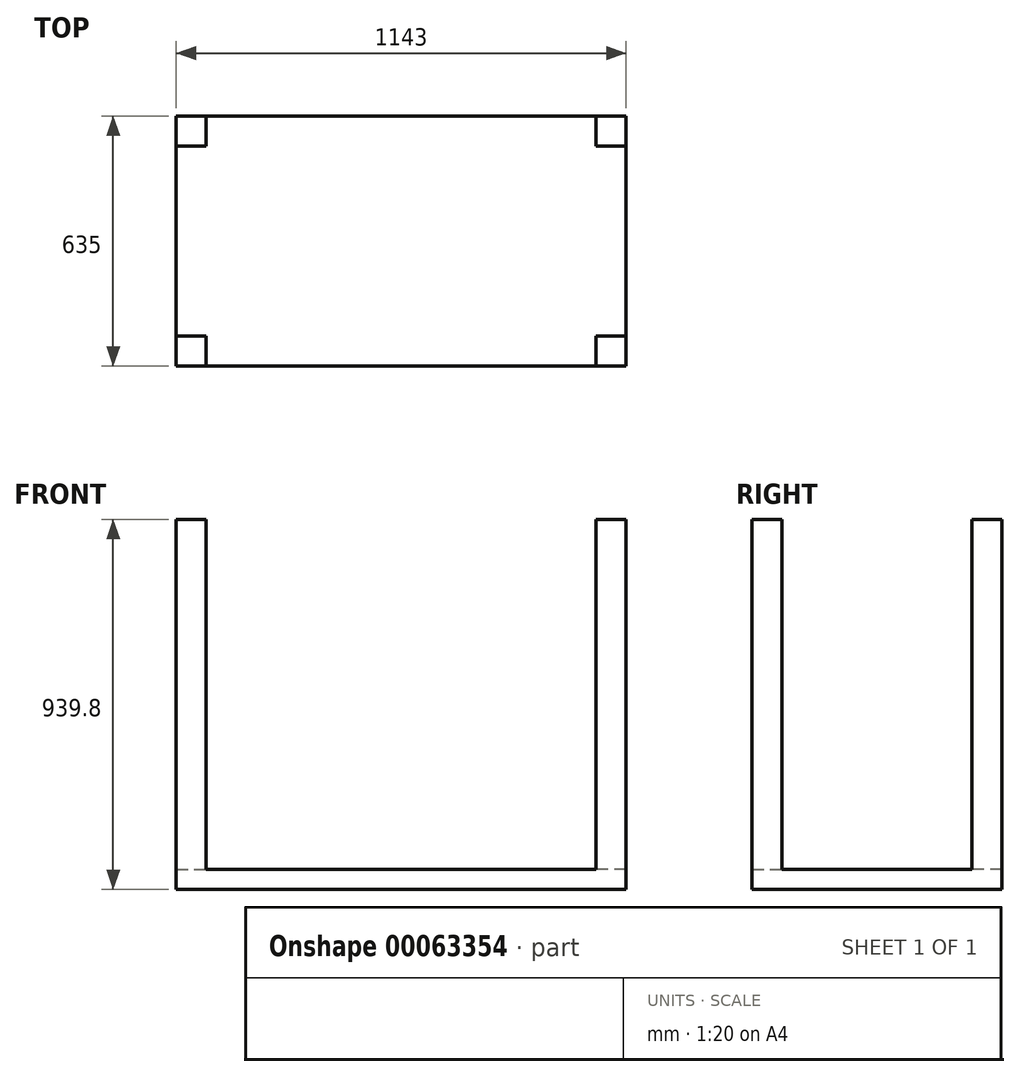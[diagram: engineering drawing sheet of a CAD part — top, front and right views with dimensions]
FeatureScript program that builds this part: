
annotation { "Feature Type Name" : "Feature", "Feature Type Description" : "" }
export const myFeature = defineFeature(function(context is Context, id is Id, definition is map)
    precondition{}
    {
        {
            var Q0;
            Q0=qCreatedBy(makeId("Top.planeOp"),FACE);
            var sketch = newSketch(context, id + "F0", { "sketchPlane" : qUnion([Q0])});
            skLineSegment(sketch, "E0.rect.bottom", {"start": v(571.5, 317.5) * mm, "end": v(-571.5, 317.5) * mm});
            skLineSegment(sketch, "E0.rect.top", {"start": v(571.5, -317.5) * mm, "end": v(-571.5, -317.5) * mm});
            skLineSegment(sketch, "E0.rect.left", {"start": v(571.5, 317.5) * mm, "end": v(571.5, -317.5) * mm});
            skLineSegment(sketch, "E0.rect.right", {"start": v(-571.5, 317.5) * mm, "end": v(-571.5, -317.5) * mm});
            skPoint(sketch, "E0.rect.middle", {"position": v(0, 0) * mm});
            skSolve(sketch);
        }
        {
            var Q0;
            Q0=makeQuery(id+"F0.imprint","IMPRINT",FACE,{"disambiguationData":[TD([[makeQuery(id+"F0.imprint","IMPRINT",EDGE,{"derivedFrom":sQuery(id+"F0.wireOp",EDGE,"E0.rect.bottom")}),1.0]])]});
            extrude(context, id + "F1", {"entities" : qUnion([Q0]), "endBound" : BoundingType.SYMMETRIC, "depth" : 50.8 * mm});
        }
        {
            var Q0;
            Q0=makeQuery(id+"F1.opExtrude","CAP_FACE",FACE,{"disambiguationData":[OSD([sQuery(id+"F0.wireOp",EDGE,"E0.rect.bottom"),sQuery(id+"F0.wireOp",EDGE,"E0.rect.top"),sQuery(id+"F0.wireOp",EDGE,"E0.rect.left"),sQuery(id+"F0.wireOp",EDGE,"E0.rect.right")])],"isStart":false});
            var sketch = newSketch(context, id + "F2", { "sketchPlane" : qUnion([Q0])});
            skLineSegment(sketch, "E1.bottom", {"start": v(-571.5, 317.5) * mm, "end": v(-495.3, 317.5) * mm});
            skLineSegment(sketch, "E1.top", {"start": v(-571.5, 241.3) * mm, "end": v(-495.3, 241.3) * mm});
            skLineSegment(sketch, "E1.left", {"start": v(-571.5, 317.5) * mm, "end": v(-571.5, 241.3) * mm});
            skLineSegment(sketch, "E1.right", {"start": v(-495.3, 317.5) * mm, "end": v(-495.3, 241.3) * mm});
            skLineSegment(sketch, "E2.bottom", {"start": v(-571.5, -317.5) * mm, "end": v(-495.3, -317.5) * mm});
            skLineSegment(sketch, "E2.top", {"start": v(-571.5, -241.3) * mm, "end": v(-495.3, -241.3) * mm});
            skLineSegment(sketch, "E2.left", {"start": v(-571.5, -317.5) * mm, "end": v(-571.5, -241.3) * mm});
            skLineSegment(sketch, "E2.right", {"start": v(-495.3, -317.5) * mm, "end": v(-495.3, -241.3) * mm});
            skLineSegment(sketch, "E3.bottom", {"start": v(571.5, 317.5) * mm, "end": v(495.3, 317.5) * mm});
            skLineSegment(sketch, "E3.top", {"start": v(571.5, 241.3) * mm, "end": v(495.3, 241.3) * mm});
            skLineSegment(sketch, "E3.left", {"start": v(571.5, 317.5) * mm, "end": v(571.5, 241.3) * mm});
            skLineSegment(sketch, "E3.right", {"start": v(495.3, 317.5) * mm, "end": v(495.3, 241.3) * mm});
            skLineSegment(sketch, "E4.bottom", {"start": v(571.5, -317.5) * mm, "end": v(495.3, -317.5) * mm});
            skLineSegment(sketch, "E4.top", {"start": v(571.5, -241.3) * mm, "end": v(495.3, -241.3) * mm});
            skLineSegment(sketch, "E4.left", {"start": v(571.5, -317.5) * mm, "end": v(571.5, -241.3) * mm});
            skLineSegment(sketch, "E4.right", {"start": v(495.3, -317.5) * mm, "end": v(495.3, -241.3) * mm});
            skSolve(sketch);
        }
        {
            var Q0;
            Q0 = qSketchRegion(id + "F2", true);
            extrude(context, id + "F3", {"entities" : qUnion([Q0]), "operationType" : NewBodyOperationType.ADD, "depth" : 889 * mm});
        }
    });
